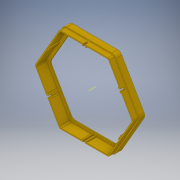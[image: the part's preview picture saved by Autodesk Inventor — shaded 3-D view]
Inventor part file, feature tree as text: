
AUTODESK INVENTOR PART (.ipt)
format: ipt  version: 2019 (Build 230136000, 136)  size: 570,880 bytes
history: native  units: mm
features: extrude x6, sketch x6, projected_geometry x4, fillet x2, other x1, pattern_circular x1
ambient origin geometry x8: Origin, YZ Plane, XZ Plane, XY Plane, X Axis, Y Axis, Z Axis, Center Point
bodies: Solid1 (feature_tree)
feature tree (20):
  extrude  "Extrusion1"  Depth=2.0mm
  extrude  "Extrusion5"  Depth=2.0mm
  extrude  "Extrusion6"  Depth=20.0mm
  fillet  "Fillet1"  [1 undecoded]
  fillet  "Fillet2"  Radius=6.0mm
  extrude  "Extrusion7"  TaperAngle=0.0deg  [1 undecoded]
  extrude  "Extrusion8"  Depth=4.0mm
  other  "Work Axis2"
  pattern_circular  "Circular Pattern1"  [2 undecoded]
  extrude  "Extrusion9"  Depth=6.5mm
  sketch  "Sketch1"  dims[d0=175.0mm d1=2.0mm]
  sketch  "Sketch5"  dims[d2=0.0mm d15=2.0mm]
  projected_geometry  "Projected Loop4"
  sketch  "Sketch7"  dims[d16=2.0mm d17=20.0mm d18=0.0mm d19=6.0mm]
  projected_geometry  "Projected Loop6"
  sketch  "Sketch8"  dims[d20=7.0mm d21=0.0mm]
  sketch  "Sketch9"  dims[d22=10.0mm d23=4.0mm]
  projected_geometry  "Projected Loop7"
  sketch  "Sketch11"  dims[d24=10.0mm d25=3.3mm d26=6.5mm d27=0.0mm d28=4.0mm d29=3.0mm d30=5.0mm d31=0.0mm d32=60.0mm d33=360.0deg d35=10.0mm d36=0.0mm]
  projected_geometry  "Projected Loop8"
note: 4 required parameter values undecoded (feature->parameter linkage not recoverable at this tier; creation-order binding heuristic only, values carry confidence <= 0.55)
